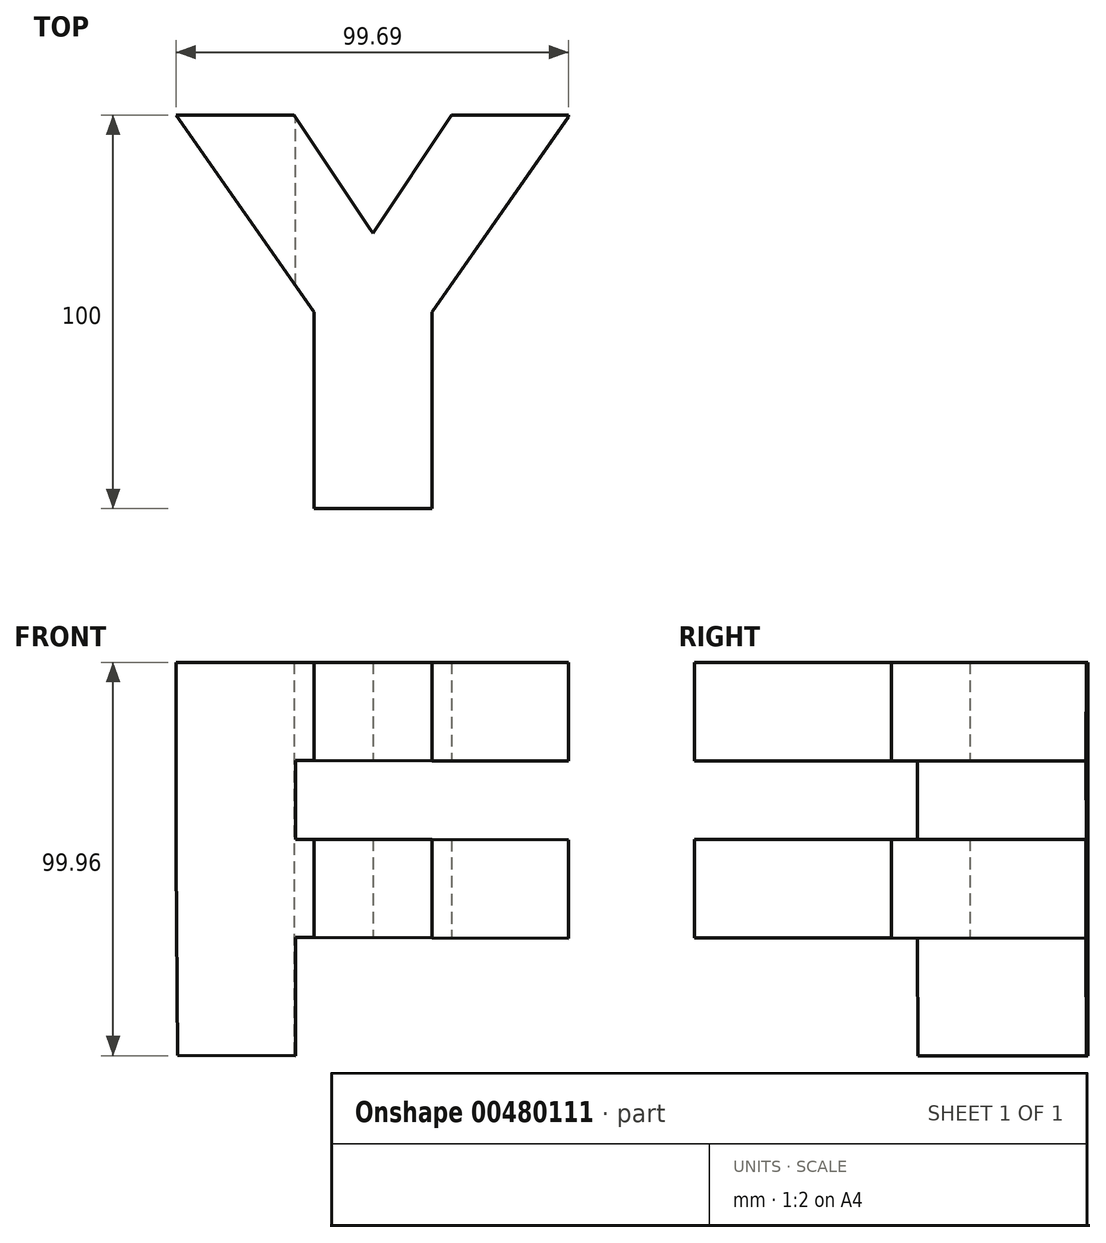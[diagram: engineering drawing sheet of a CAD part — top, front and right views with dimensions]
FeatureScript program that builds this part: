
annotation { "Feature Type Name" : "Feature", "Feature Type Description" : "" }
export const myFeature = defineFeature(function(context is Context, id is Id, definition is map)
    precondition{}
    {
        {
            var Q0;
            Q0=qCreatedBy(makeId("Top.planeOp"),FACE);
            var sketch = newSketch(context, id + "F0", { "sketchPlane" : qUnion([Q0])});
            skLineSegment(sketch, "E0.bottom", {"start": v(50, 50) * mm, "end": v(20, 50) * mm, "construction": true});
            skLineSegment(sketch, "E0.top", {"start": v(15, -50) * mm, "end": v(-15, -50) * mm, "construction": true});
            skPoint(sketch, "E0.middle", {"position": v(0, 0) * mm});
            skLineSegment(sketch, "E1", {"start": v(-50, 50) * mm, "end": v(-20, 50) * mm});
            skLineSegment(sketch, "E2", {"start": v(50, 50) * mm, "end": v(20, 50) * mm});
            skLineSegment(sketch, "E3", {"start": v(-20, 50) * mm, "end": v(0, 20) * mm});
            skLineSegment(sketch, "E4", {"start": v(0, 20) * mm, "end": v(20, 50) * mm});
            skLineSegment(sketch, "E5", {"start": v(-50, 50) * mm, "end": v(-15, 0) * mm});
            skLineSegment(sketch, "E6", {"start": v(50, 50) * mm, "end": v(15, 0) * mm});
            skLineSegment(sketch, "E7.top", {"start": v(-15, -50) * mm, "end": v(15, -50) * mm});
            skLineSegment(sketch, "E7.left", {"start": v(-15, 0) * mm, "end": v(-15, -50) * mm});
            skLineSegment(sketch, "E7.right", {"start": v(15, 0) * mm, "end": v(15, -50) * mm});
            skLineSegment(sketch, "E8.trimOffspring", {"start": v(-20, 50) * mm, "end": v(-50, 50) * mm, "construction": true});
            skPoint(sketch, "E9.orphan", {"position": v(-50, -50) * mm});
            skPoint(sketch, "E0.left.end.orphan", {"position": v(50, -50) * mm});
            skSolve(sketch);
        }
        {
            var Q0;
            Q0=qCreatedBy(makeId("Front.planeOp"),FACE);
            var sketch = newSketch(context, id + "F1", { "sketchPlane" : qUnion([Q0])});
            skLineSegment(sketch, "E10.bottom", {"start": v(49.7, 49.89) * mm, "end": v(-50.3, 50.1) * mm, "construction": true});
            skLineSegment(sketch, "E10.right", {"start": v(-50.3, 50.1) * mm, "end": v(-49.7, -49.89) * mm, "construction": true});
            skPoint(sketch, "E10.middle", {"position": v(0, 0) * mm});
            skLineSegment(sketch, "E11", {"start": v(-50.3, 50.1) * mm, "end": v(-49.7, -49.89) * mm});
            skLineSegment(sketch, "E12", {"start": v(-50.3, 50.1) * mm, "end": v(49.7, 49.89) * mm});
            skLineSegment(sketch, "E13", {"start": v(49.7, 49.89) * mm, "end": v(49.64, 24.9) * mm});
            skLineSegment(sketch, "E14", {"start": v(49.64, 24.9) * mm, "end": v(-19.63, 25.04) * mm});
            skLineSegment(sketch, "E15", {"start": v(-19.63, 25.04) * mm, "end": v(-19.67, 5.04) * mm});
            skLineSegment(sketch, "E16", {"start": v(-19.67, 5.04) * mm, "end": v(49.64, 4.9) * mm});
            skLineSegment(sketch, "E17", {"start": v(49.64, 4.9) * mm, "end": v(49.64, -20.1) * mm});
            skLineSegment(sketch, "E18", {"start": v(49.64, -20.1) * mm, "end": v(-19.63, -19.96) * mm});
            skLineSegment(sketch, "E19", {"start": v(-19.63, -19.96) * mm, "end": v(-19.7, -49.96) * mm});
            skLineSegment(sketch, "E20", {"start": v(-19.7, -49.96) * mm, "end": v(-49.7, -49.89) * mm});
            skSolve(sketch);
        }
        {
            var Q0;
            Q0 = qSketchRegion(id + "F0", true);
            extrude(context, id + "F2", {"entities" : qUnion([Q0]), "endBound" : BoundingType.SYMMETRIC, "depth" : 100 * mm});
        }
        {
            var Q0;
            Q0 = qSketchRegion(id + "F1", true);
            extrude(context, id + "F3", {"entities" : qUnion([Q0]), "operationType" : NewBodyOperationType.INTERSECT, "endBound" : BoundingType.SYMMETRIC, "depth" : 100 * mm});
        }
    });
